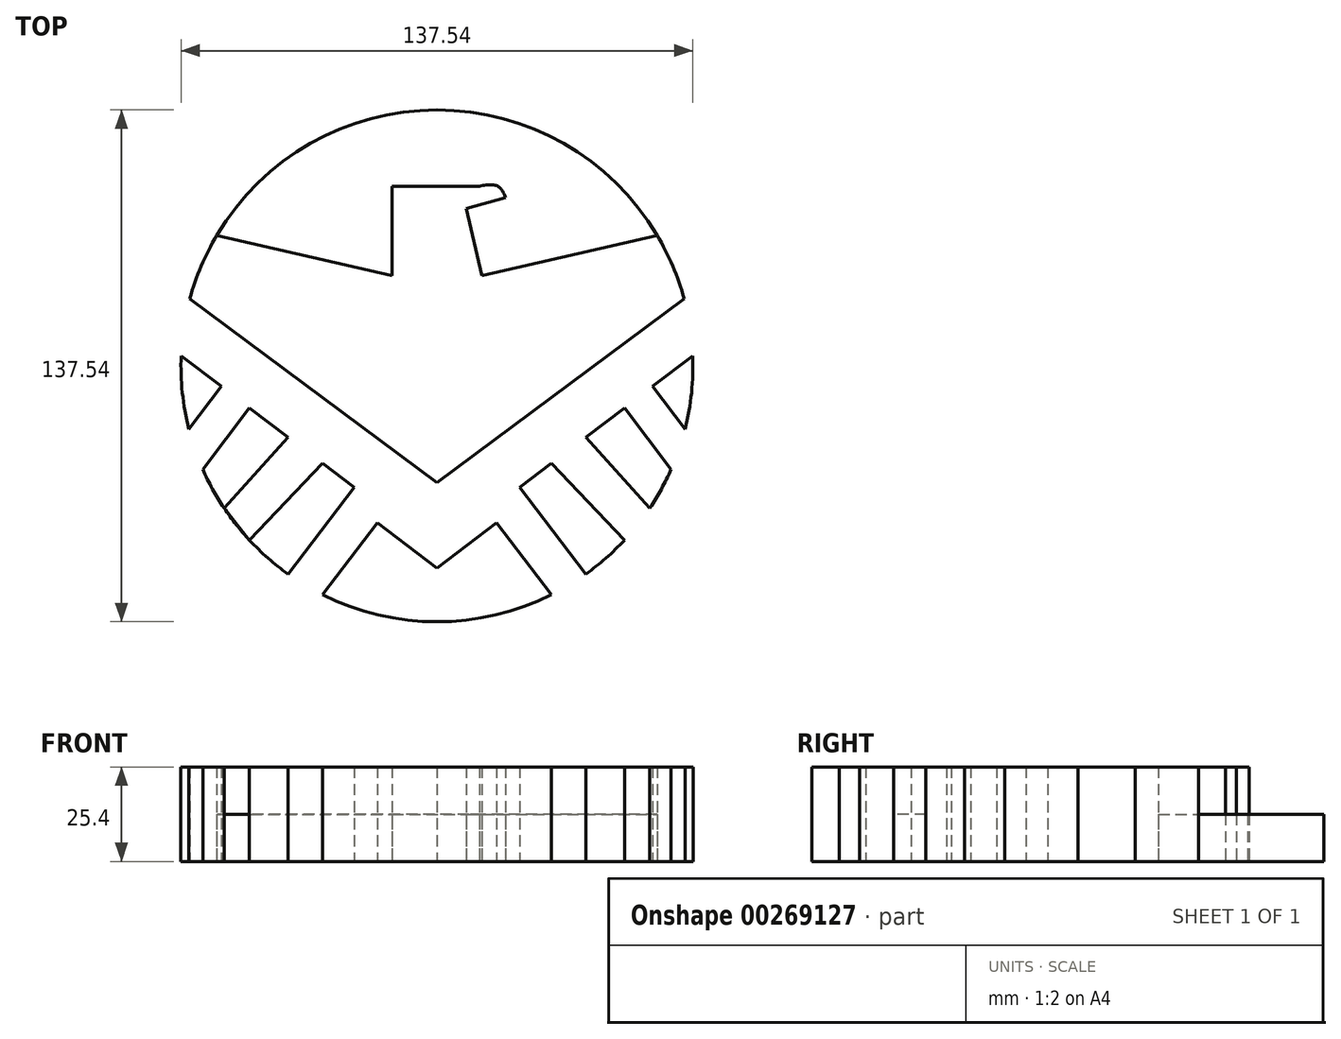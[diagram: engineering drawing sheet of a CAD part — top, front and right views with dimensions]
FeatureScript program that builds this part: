
annotation { "Feature Type Name" : "Feature", "Feature Type Description" : "" }
export const myFeature = defineFeature(function(context is Context, id is Id, definition is map)
    precondition{}
    {
        {
            var Q0;
            Q0=qCreatedBy(makeId("Top.planeOp"),FACE);
            var sketch = newSketch(context, id + "F0", { "sketchPlane" : qUnion([Q0])});
            skCircle(sketch, "E0", {"center": v(0, 0) * mm, "radius": 76.05 * mm});
            skArc(sketch, "E1", {"start": v(-62.92, -27.76) * mm, "mid": v(65, 22.45) * mm, "end": v(-66.64, -16.98) * mm});
            skLineSegment(sketch, "E2", {"start": v(0, -31.39) * mm, "end": v(-66.37, 18.01) * mm});
            skLineSegment(sketch, "E3", {"start": v(-68.72, 2.72) * mm, "end": v(-57.91, -5.5) * mm});
            skLineSegment(sketch, "E4", {"start": v(-57.91, -5.5) * mm, "end": v(-66.64, -16.98) * mm});
            skLineSegment(sketch, "E5", {"start": v(-62.92, -27.76) * mm, "end": v(-50.36, -11.24) * mm});
            skLineSegment(sketch, "E6", {"start": v(-50.36, -11.24) * mm, "end": v(-39.97, -19.15) * mm});
            skLineSegment(sketch, "E7", {"start": v(-57.2, -38.19) * mm, "end": v(-50.36, -46.83) * mm});
            skLineSegment(sketch, "E8", {"start": v(-57.2, -38.19) * mm, "end": v(-39.97, -19.15) * mm});
            skLineSegment(sketch, "E9", {"start": v(-39.97, -55.97) * mm, "end": v(-22.23, -32.64) * mm});
            skLineSegment(sketch, "E10", {"start": v(-50.36, -46.83) * mm, "end": v(-30.76, -26.15) * mm});
            skLineSegment(sketch, "E11.MirrorCS", {"start": v(57.91, -5.5) * mm, "end": v(66.64, -16.98) * mm});
            skLineSegment(sketch, "E12.MirrorCS", {"start": v(62.92, -27.76) * mm, "end": v(50.36, -11.24) * mm});
            skLineSegment(sketch, "E13.MirrorCS", {"start": v(57.2, -38.19) * mm, "end": v(39.97, -19.15) * mm});
            skLineSegment(sketch, "E14.MirrorCS", {"start": v(50.36, -46.83) * mm, "end": v(30.76, -26.15) * mm});
            skLineSegment(sketch, "E15.MirrorCS", {"start": v(39.97, -55.97) * mm, "end": v(22.23, -32.64) * mm});
            skLineSegment(sketch, "E16.MirrorCS", {"start": v(50.36, -11.24) * mm, "end": v(39.97, -19.15) * mm});
            skLineSegment(sketch, "E17.MirrorCS", {"start": v(68.72, 2.72) * mm, "end": v(57.91, -5.5) * mm});
            skArc(sketch, "E18.MirrorCS", {"start": v(62.92, -27.76) * mm, "mid": v(-65, 22.45) * mm, "end": v(66.64, -16.98) * mm});
            skLineSegment(sketch, "E19.MirrorCS", {"start": v(0, -31.39) * mm, "end": v(66.37, 18.01) * mm});
            skLineSegment(sketch, "E20.trimOffspring", {"start": v(-30.76, -26.15) * mm, "end": v(-22.23, -32.64) * mm});
            skLineSegment(sketch, "E21.trimOffspring", {"start": v(30.76, -26.15) * mm, "end": v(22.23, -32.64) * mm});
            skPoint(sketch, "E22.orphan", {"position": v(0, -49.54) * mm});
            skLineSegment(sketch, "E23", {"start": v(22.23, -32.64) * mm, "end": v(30.76, -26.15) * mm});
            skLineSegment(sketch, "E24", {"start": v(-16, -42.16) * mm, "end": v(0, -54.33) * mm});
            skLineSegment(sketch, "E25", {"start": v(-16, -42.16) * mm, "end": v(-30.73, -61.53) * mm});
            skLineSegment(sketch, "E26.MirrorCS", {"start": v(16, -42.16) * mm, "end": v(0, -54.33) * mm});
            skLineSegment(sketch, "E27.MirrorCS", {"start": v(16, -42.16) * mm, "end": v(30.73, -61.53) * mm});
            skLineSegment(sketch, "E28.trimOffspring", {"start": v(39.97, -19.15) * mm, "end": v(50.36, -11.24) * mm});
            skLineSegment(sketch, "E29.trimOffspring", {"start": v(57.91, -5.5) * mm, "end": v(68.72, 2.72) * mm});
            skLineSegment(sketch, "E30", {"start": v(-59.13, 35.11) * mm, "end": v(-12, 24.3) * mm});
            skLineSegment(sketch, "E31", {"start": v(12, 24.3) * mm, "end": v(59.13, 35.11) * mm});
            skLineSegment(sketch, "E32", {"start": v(-12, 24.3) * mm, "end": v(-12, 48.31) * mm});
            skLineSegment(sketch, "E33", {"start": v(-12, 48.31) * mm, "end": v(11.39, 48.31) * mm});
            skLineSegment(sketch, "E34", {"start": v(12, 24.3) * mm, "end": v(7.87, 42.32) * mm});
            skFitSpline(sketch, "E35", {"points": [v(11.39, 48.31) * mm, v(16.3, 48.31) * mm, v(18.46, 45.24) * mm], "startDerivative": vector(10.45, 1.76) * mm, "endDerivative": vector(3.55, -8.14) * mm});
            skLineSegment(sketch, "E36", {"start": v(7.87, 42.32) * mm, "end": v(18.46, 45.24) * mm});
            skPoint(sketch, "E37.orphan", {"position": v(0, 21.54) * mm});
            skSolve(sketch);
        }
        {
            var Q0;
            {var subQ3=sQuery(id+"F0.wireOp",EDGE,"E2");Q0=makeQuery(id+"F0.imprint","IMPRINT",FACE,{"disambiguationData":[TD([[makeQuery(id+"F0.imprint","IMPRINT",EDGE,{"derivedFrom":subQ3}),-1.0]])]});}
            var Q1;
            {var subQ0=sQuery(id+"F0.wireOp",EDGE,"E5");Q1=makeQuery(id+"F0.imprint","IMPRINT",FACE,{"disambiguationData":[TD([[makeQuery(id+"F0.imprint","IMPRINT",EDGE,{"derivedFrom":subQ0}),-1.0]])]});}
            var Q2;
            {var subQ0=sQuery(id+"F0.wireOp",EDGE,"E4");Q2=makeQuery(id+"F0.imprint","IMPRINT",FACE,{"disambiguationData":[TD([[makeQuery(id+"F0.imprint","IMPRINT",EDGE,{"derivedFrom":subQ0}),-1.0]])]});}
            var Q3;
            {var subQ0=sQuery(id+"F0.wireOp",EDGE,"E9");Q3=makeQuery(id+"F0.imprint","IMPRINT",FACE,{"disambiguationData":[TD([[makeQuery(id+"F0.imprint","IMPRINT",EDGE,{"derivedFrom":subQ0}),1.0]])]});}
            var Q4;
            Q4=makeQuery(id+"F0.imprint","IMPRINT",FACE,{"disambiguationData":[TD([[makeQuery(id+"F0.imprint","IMPRINT",EDGE,{"derivedFrom":sQuery(id+"F0.wireOp",EDGE,"E24")}),-1.0]])]});
            var Q5;
            {var subQ0=sQuery(id+"F0.wireOp",EDGE,"E14.MirrorCS");Q5=makeQuery(id+"F0.imprint","IMPRINT",FACE,{"disambiguationData":[TD([[makeQuery(id+"F0.imprint","IMPRINT",EDGE,{"derivedFrom":subQ0}),1.0]])]});}
            var Q6;
            {var subQ0=sQuery(id+"F0.wireOp",EDGE,"E12.MirrorCS");Q6=makeQuery(id+"F0.imprint","IMPRINT",FACE,{"disambiguationData":[TD([[makeQuery(id+"F0.imprint","IMPRINT",EDGE,{"derivedFrom":subQ0}),1.0]])]});}
            var Q7;
            {var subQ0=sQuery(id+"F0.wireOp",EDGE,"E11.MirrorCS");Q7=makeQuery(id+"F0.imprint","IMPRINT",FACE,{"disambiguationData":[TD([[makeQuery(id+"F0.imprint","IMPRINT",EDGE,{"derivedFrom":subQ0}),1.0]])]});}
            extrude(context, id + "F1", {"entities" : qUnion([Q0, Q1, Q2, Q3, Q4, Q5, Q6, Q7]), "depth" : 25.4 * mm});
        }
        {
            var Q0;
            {var subQ1=sQuery(id+"F0.wireOp",EDGE,"E30");Q0=makeQuery(id+"F0.imprint","IMPRINT",FACE,{"disambiguationData":[TD([[makeQuery(id+"F0.imprint","IMPRINT",EDGE,{"derivedFrom":subQ1}),1.0]])]});}
            var Q1;
            Q1=makeQuery(id+"F0.imprint","IMPRINT",FACE,{"disambiguationData":[TD([[makeQuery(id+"F0.imprint","IMPRINT",EDGE,{"derivedFrom":sQuery(id+"F0.wireOp",EDGE,"E1")}),1.0]])]});
            extrude(context, id + "F2", {"entities" : qUnion([Q0, Q1]), "depth" : 12.7 * mm});
        }
    });
